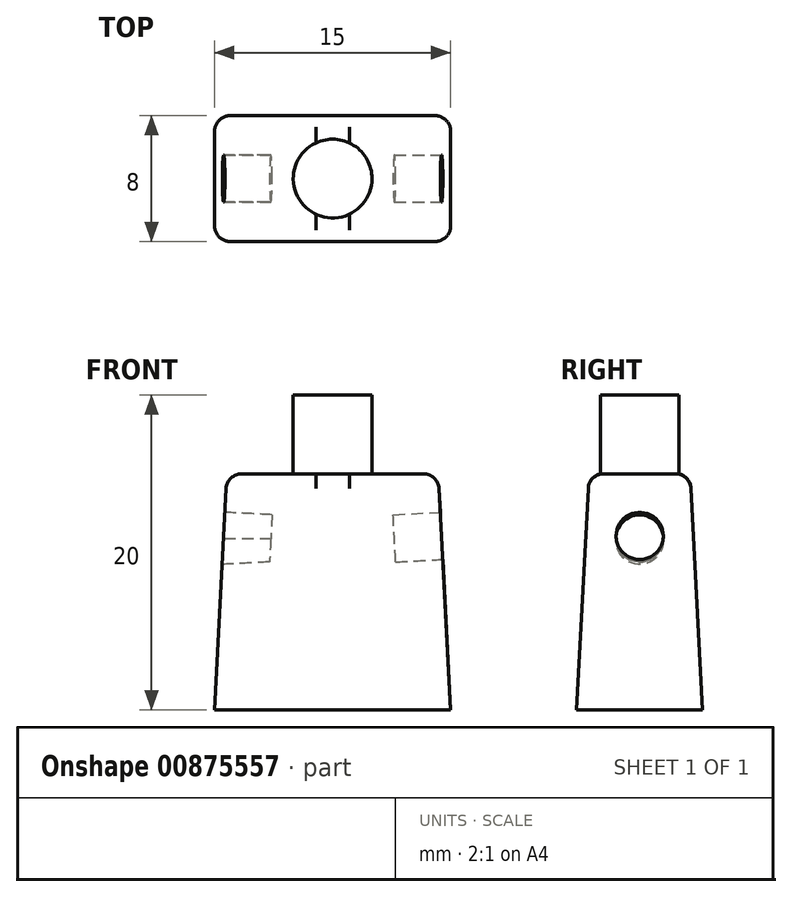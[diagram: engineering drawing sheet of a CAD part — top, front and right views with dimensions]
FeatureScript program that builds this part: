
annotation { "Feature Type Name" : "Feature", "Feature Type Description" : "" }
export const myFeature = defineFeature(function(context is Context, id is Id, definition is map)
    precondition{}
    {
        {
            var Q0;
            Q0=qCreatedBy(makeId("Top.planeOp"),FACE);
            var sketch = newSketch(context, id + "F0", { "sketchPlane" : qUnion([Q0])});
            skLineSegment(sketch, "E0.bottom", {"start": v(7.5, 4) * mm, "end": v(-7.5, 4) * mm});
            skLineSegment(sketch, "E0.top", {"start": v(7.5, -4) * mm, "end": v(-7.5, -4) * mm});
            skLineSegment(sketch, "E0.left", {"start": v(7.5, 4) * mm, "end": v(7.5, -4) * mm});
            skLineSegment(sketch, "E0.right", {"start": v(-7.5, 4) * mm, "end": v(-7.5, -4) * mm});
            skPoint(sketch, "E0.middle", {"position": v(0, 0) * mm});
            skSolve(sketch);
        }
        {
            var Q0;
            Q0=makeQuery(id+"F0.imprint","IMPRINT",FACE,{"disambiguationData":[TD([[makeQuery(id+"F0.imprint","IMPRINT",EDGE,{"derivedFrom":sQuery(id+"F0.wireOp",EDGE,"E0.bottom")}),1.0]])]});
            extrude(context, id + "F1", {"entities" : qUnion([Q0]), "depth" : 15 * mm, "offsetDistance" : 25 * mm, "hasDraft" : true, "draftAngle" : 3 * degree, "draftPullDirection" : true});
        }
        {
            var Q0;
            Q0=makeQuery(id+"F1.opExtrude","CAP_FACE",FACE,{"disambiguationData":[OSD([sQuery(id+"F0.wireOp",EDGE,"E0.bottom"),sQuery(id+"F0.wireOp",EDGE,"E0.top"),sQuery(id+"F0.wireOp",EDGE,"E0.left"),sQuery(id+"F0.wireOp",EDGE,"E0.right")])],"isStart":false});
            var sketch = newSketch(context, id + "F2", { "sketchPlane" : qUnion([Q0])});
            skCircle(sketch, "E1", {"center": v(0, 0) * mm, "radius": 2.5 * mm});
            skSolve(sketch);
        }
        {
            var Q0;
            Q0 = qSketchRegion(id + "F2", true);
            extrude(context, id + "F3", {"entities" : qUnion([Q0]), "operationType" : NewBodyOperationType.ADD, "depth" : 5 * mm, "offsetDistance" : 25 * mm});
        }
        {
            var Q0;
            Q0=makeQuery(id+"F1.opExtrude","CAP_EDGE",EDGE,{"disambiguationData":[OSD([sQuery(id+"F0.wireOp",EDGE,"E0.bottom")])],"isStart":false});
            var Q1;
            Q1=makeQuery(id+"F1.opExtrude","SWEPT_EDGE",EDGE,{"disambiguationData":[OSD([sQuery(id+"F0.wireOp",EDGE,"E0.bottom"),sQuery(id+"F0.wireOp",EDGE,"E0.right")])]});
            var Q2;
            Q2=makeQuery(id+"F1.opExtrude","SWEPT_EDGE",EDGE,{"disambiguationData":[OSD([sQuery(id+"F0.wireOp",EDGE,"E0.bottom"),sQuery(id+"F0.wireOp",EDGE,"E0.left")])]});
            var Q3;
            Q3=makeQuery(id+"F1.opExtrude","SWEPT_EDGE",EDGE,{"disambiguationData":[OSD([sQuery(id+"F0.wireOp",EDGE,"E0.top"),sQuery(id+"F0.wireOp",EDGE,"E0.right")])]});
            var Q4;
            Q4=makeQuery(id+"F1.opExtrude","CAP_EDGE",EDGE,{"disambiguationData":[OSD([sQuery(id+"F0.wireOp",EDGE,"E0.right")])],"isStart":false});
            var Q5;
            Q5=makeQuery(id+"F1.opExtrude","CAP_EDGE",EDGE,{"disambiguationData":[OSD([sQuery(id+"F0.wireOp",EDGE,"E0.top")])],"isStart":false});
            var Q6;
            Q6=makeQuery(id+"F1.opExtrude","SWEPT_EDGE",EDGE,{"disambiguationData":[OSD([sQuery(id+"F0.wireOp",EDGE,"E0.top"),sQuery(id+"F0.wireOp",EDGE,"E0.left")])]});
            var Q7;
            Q7=makeQuery(id+"F1.opExtrude","CAP_EDGE",EDGE,{"disambiguationData":[OSD([sQuery(id+"F0.wireOp",EDGE,"E0.left")])],"isStart":false});
            fillet(context, id + "F4", {"entities" : qUnion([Q0, Q1, Q2, Q3, Q4, Q5, Q6, Q7]), "radius" : 1 * mm, "tangentPropagation" : true, "allowEdgeOverflow" : false});
        }
        {
            var Q0;
            Q0=makeQuery(id+"F1.opExtrude","SWEPT_FACE",FACE,{"disambiguationData":[OSD([sQuery(id+"F0.wireOp",EDGE,"E0.right")])]});
            var sketch = newSketch(context, id + "F5", { "sketchPlane" : qUnion([Q0])});
            skCircle(sketch, "E2", {"center": v(0, 10.68) * mm, "radius": 1.5 * mm});
            skSolve(sketch);
        }
        {
            var Q0;
            Q0=makeQuery(id+"F5.imprint","IMPRINT",FACE,{"disambiguationData":[TD([[makeQuery(id+"F5.imprint","IMPRINT",EDGE,{"derivedFrom":sQuery(id+"F5.wireOp",EDGE,"E2")}),1.0]])]});
            extrude(context, id + "F6", {"entities" : qUnion([Q0]), "operationType" : NewBodyOperationType.REMOVE, "oppositeDirection" : true, "depth" : 3 * mm, "offsetDistance" : 25 * mm});
        }
        {
            var Q0;
            Q0=makeQuery(id+"F1.opExtrude","SWEPT_FACE",FACE,{"disambiguationData":[OSD([sQuery(id+"F0.wireOp",EDGE,"E0.left")])]});
            var sketch = newSketch(context, id + "F7", { "sketchPlane" : qUnion([Q0])});
            skCircle(sketch, "E3", {"center": v(0, 10.68) * mm, "radius": 1.5 * mm});
            skSolve(sketch);
        }
        {
            var Q0;
            Q0=makeQuery(id+"F7.imprint","IMPRINT",FACE,{"disambiguationData":[TD([[makeQuery(id+"F7.imprint","IMPRINT",EDGE,{"derivedFrom":sQuery(id+"F7.wireOp",EDGE,"E3")}),1.0]])]});
            var Q1;
            Q1=makeQuery(id+"F6.boolean.opBoolean","COPY",FACE,{"derivedFrom":makeQuery(id+"F6.opExtrude","CAP_FACE",FACE,{"disambiguationData":[OSD([sQuery(id+"F5.wireOp",EDGE,"E2")])],"isStart":false})});
            extrude(context, id + "F8", {"entities" : qUnion([Q0, Q1]), "operationType" : NewBodyOperationType.REMOVE, "oppositeDirection" : true, "depth" : 3 * mm, "offsetDistance" : 25 * mm});
        }
    });
